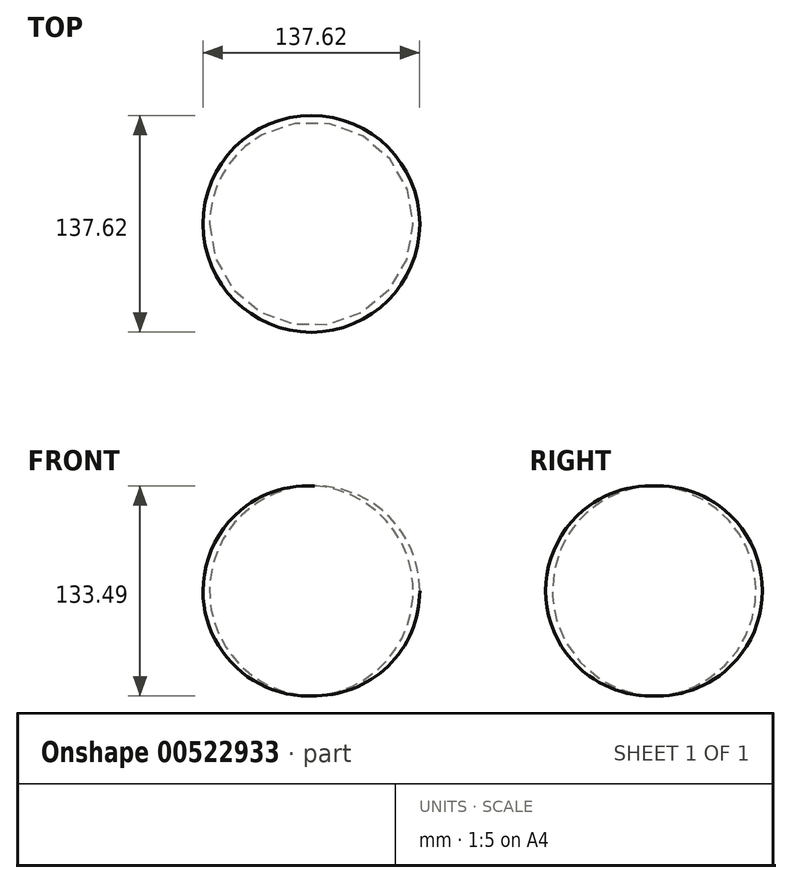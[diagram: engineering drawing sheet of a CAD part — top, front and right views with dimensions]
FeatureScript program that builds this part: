
annotation { "Feature Type Name" : "Feature", "Feature Type Description" : "" }
export const myFeature = defineFeature(function(context is Context, id is Id, definition is map)
    precondition{}
    {
        {
            var Q0;
            Q0=qCreatedBy(makeId("Front.planeOp"),FACE);
            var sketch = newSketch(context, id + "F0", { "sketchPlane" : qUnion([Q0])});
            skArc(sketch, "E0", {"start": v(0, -76.76) * mm, "mid": v(68.81, -10.05) * mm, "end": v(0, 56.66) * mm});
            skLineSegment(sketch, "E1", {"start": v(0, 80.02) * mm, "end": v(0, -79.98) * mm});
            skSolve(sketch);
        }
        {
            var Q0;
            Q0=makeQuery(id+"F0.imprint","IMPRINT",FACE,{"disambiguationData":[TD([[makeQuery(id+"F0.imprint","IMPRINT",EDGE,{"derivedFrom":sQuery(id+"F0.wireOp",EDGE,"E0")}),1.0]])]});
            var Q1;
            Q1=sQuery(id+"F0.wireOp",EDGE,"E1");
            revolve(context, id + "F1", {"entities" : qUnion([Q0]), "axis" : qUnion([Q1]), "revolveType" : RevolveType.FULL});
        }
    });
